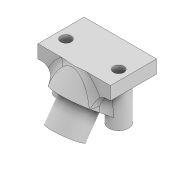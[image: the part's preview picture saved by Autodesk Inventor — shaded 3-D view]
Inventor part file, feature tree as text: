
AUTODESK INVENTOR PART (.ipt)
format: ipt  version: 2022 (Build 260153000, 153)  size: 377,856 bytes
history: native  units: mm
features: extrude x9, sketch x6, plane x2, projected_geometry x2, fillet x1
ambient origin geometry x8: Origin, YZ Plane, XZ Plane, XY Plane, X Axis, Y Axis, Z Axis, Center Point
bodies: Body1 (feature_tree)
feature tree (20):
  sketch  "Sketch6"  dims[d29=22.0mm d30=14.0mm]
  extrude  "Extrusion6"  Depth=14.0mm
  plane  "Work Plane3"
  extrude  "Extrusion7"  [1 undecoded]
  extrude  "Extrusion9"  Depth=5.0mm
  plane  "Work Plane4"
  extrude  "Extrusion25"  Depth=9.8mm
  extrude  "Extrusion19"  Depth=3.2mm
  extrude  "Extrusion20"  Depth=5.5mm
  extrude  "Extrusion22"  Depth=5.5mm
  extrude  "Extrusion23"  Depth=3.0mm
  extrude  "Extrusion26"  Depth=3.0mm
  fillet  "Fillet10"  Radius=10.0mm
  sketch  "Sketch7"  dims[d31=4.0mm d32=0.0mm d33=-6.108652mm]
  sketch  "Sketch9"  dims[d34=3.0mm d35=5.0mm]
  projected_geometry  "Projected Loop8"
  sketch  "Sketch22"  dims[d36=11.0mm d37=9.8mm]
  sketch  "Sketch26"  dims[d38=12.0mm d39=0.0mm d43=3.2mm]
  projected_geometry  "Projected Loop11"
  sketch  "Sketch27"  dims[d44=3.2mm d45=5.5mm d46=5.5mm d47=3.0mm d48=3.0mm d49=10.0mm d50=0.0mm d51=20.0mm d52=0.0mm d66=-12.0mm d87=12.2mm d88=15.0mm d89=8.0mm d90=0.0mm d91=4.0mm d92=20.0mm d93=0.0mm d94=0.0mm d97=100.0mm d98=0.0mm d99=100.0mm d100=0.0mm d105=6.0mm d106=6.0mm d107=10.0mm d108=0.0mm d109=100.0mm d110=0.0mm d116=3.0mm d12=0.5mm d13=0.872665mm d14=0.5mm d15=0.872665mm d84=0.5mm d85=0.872665mm d86=0.5mm d112=0.5mm d113=0.872665mm d114=0.5mm d115=0.872665mm]
note: 1 required parameter value undecoded (feature->parameter linkage not recoverable at this tier; creation-order binding heuristic only, values carry confidence <= 0.55)
